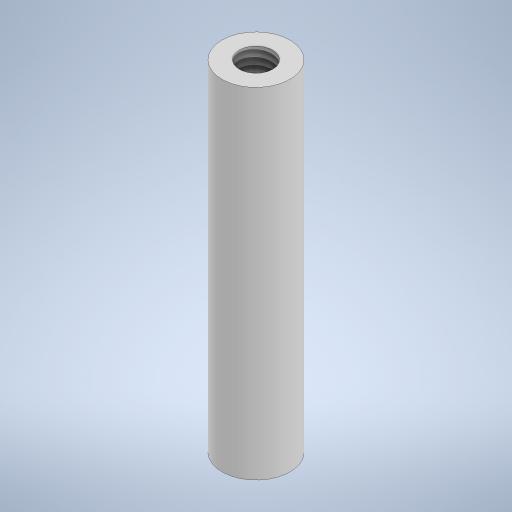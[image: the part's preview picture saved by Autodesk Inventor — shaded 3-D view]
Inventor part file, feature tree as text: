
AUTODESK INVENTOR PART (.ipt)
format: ipt  version: 2023 (Build 270158000, 158)  size: 231,424 bytes
history: native  units: in
note: dims shown in document units (in); Inventor stores cm internally (conversion verified against a paired STEP export)
features: sketch x2, extrude x1, hole x1, projected_geometry x1
ambient origin geometry x8: Origin, YZ Plane, XZ Plane, XY Plane, X Axis, Y Axis, Z Axis, Center Point
bodies: Solid1 (feature_tree)
feature tree (5):
  extrude  "Extrusion1"  Depth=0.9843in TaperAngle=0.0deg
  hole  "Hole1"  [1 undecoded]
  sketch  "Sketch1"  dims[d0=0.1969in d1=0.9843in d2=0.0in]
  sketch  "Sketch2"  dims[d3=0.0968in d4=0.9843in d5=0.1575in d6=0.0787in d7=90.0deg d8=0.315in d9=0.8108in]
  projected_geometry  "Projected Loop1"
note: 1 required parameter value undecoded (feature->parameter linkage not recoverable at this tier; creation-order binding heuristic only, values carry confidence <= 0.55)
